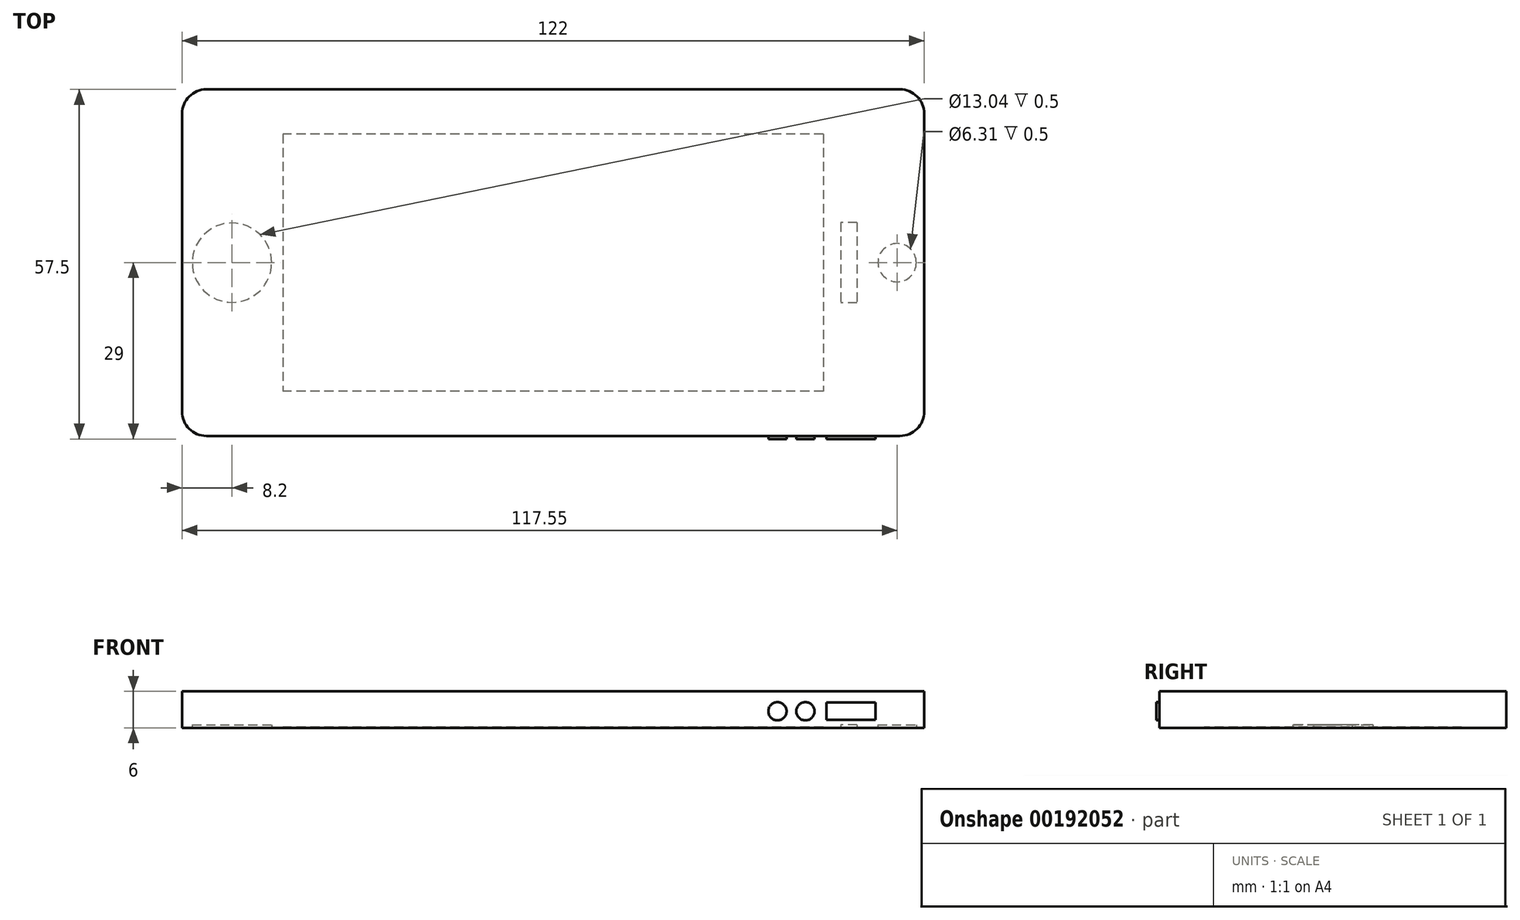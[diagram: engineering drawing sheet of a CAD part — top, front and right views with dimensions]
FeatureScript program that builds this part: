
annotation { "Feature Type Name" : "Feature", "Feature Type Description" : "" }
export const myFeature = defineFeature(function(context is Context, id is Id, definition is map)
    precondition{}
    {
        {
            var Q0;
            Q0=qCreatedBy(makeId("Top.planeOp"),FACE);
            var sketch = newSketch(context, id + "F0", { "sketchPlane" : qUnion([Q0])});
            skLineSegment(sketch, "E0.bottom", {"start": v(-61, 28.5) * mm, "end": v(61, 28.5) * mm});
            skLineSegment(sketch, "E0.top", {"start": v(-61, -28.5) * mm, "end": v(61, -28.5) * mm});
            skLineSegment(sketch, "E0.left", {"start": v(-61, 28.5) * mm, "end": v(-61, -28.5) * mm});
            skLineSegment(sketch, "E0.right", {"start": v(61, 28.5) * mm, "end": v(61, -28.5) * mm});
            skPoint(sketch, "E0.middle", {"position": v(0, 0) * mm});
            skSolve(sketch);
        }
        {
            var Q0;
            Q0=makeQuery(id+"F0.imprint","IMPRINT",FACE,{"disambiguationData":[TD([[makeQuery(id+"F0.imprint","IMPRINT",EDGE,{"derivedFrom":sQuery(id+"F0.wireOp",EDGE,"E0.bottom")}),-1.0]])]});
            extrude(context, id + "F1", {"entities" : qUnion([Q0]), "depth" : 6 * mm});
        }
        {
            var Q0;
            Q0=makeQuery(id+"F1.opExtrude","SWEPT_EDGE",EDGE,{"disambiguationData":[OSD([sQuery(id+"F0.wireOp",EDGE,"E0.bottom"),sQuery(id+"F0.wireOp",EDGE,"E0.right")])]});
            var Q1;
            Q1=makeQuery(id+"F1.opExtrude","SWEPT_EDGE",EDGE,{"disambiguationData":[OSD([sQuery(id+"F0.wireOp",EDGE,"E0.top"),sQuery(id+"F0.wireOp",EDGE,"E0.right")])]});
            var Q2;
            Q2=makeQuery(id+"F1.opExtrude","SWEPT_EDGE",EDGE,{"disambiguationData":[OSD([sQuery(id+"F0.wireOp",EDGE,"E0.bottom"),sQuery(id+"F0.wireOp",EDGE,"E0.left")])]});
            var Q3;
            Q3=makeQuery(id+"F1.opExtrude","SWEPT_EDGE",EDGE,{"disambiguationData":[OSD([sQuery(id+"F0.wireOp",EDGE,"E0.top"),sQuery(id+"F0.wireOp",EDGE,"E0.left")])]});
            fillet(context, id + "F2", {"entities" : qUnion([Q0, Q1, Q2, Q3]), "radius" : 4 * mm, "tangentPropagation" : true, "allowEdgeOverflow" : false});
        }
        {
            var Q0;
            Q0=makeQuery(id+"F1.opExtrude","SWEPT_FACE",FACE,{"disambiguationData":[OSD([sQuery(id+"F0.wireOp",EDGE,"E0.top")])]});
            var sketch = newSketch(context, id + "F3", { "sketchPlane" : qUnion([Q0])});
            skLineSegment(sketch, "E1.bottom", {"start": v(52.97, 1.29) * mm, "end": v(44.92, 1.29) * mm});
            skLineSegment(sketch, "E1.top", {"start": v(52.97, 4.16) * mm, "end": v(44.92, 4.16) * mm});
            skLineSegment(sketch, "E1.left", {"start": v(52.97, 1.29) * mm, "end": v(52.97, 4.16) * mm});
            skLineSegment(sketch, "E1.right", {"start": v(44.92, 1.29) * mm, "end": v(44.92, 4.16) * mm});
            skPoint(sketch, "E1.middle", {"position": v(48.94, 2.73) * mm});
            skCircle(sketch, "E2", {"center": v(41.47, 2.73) * mm, "radius": 1.5 * mm});
            skPoint(sketch, "E2.centerSnap0", {"position": v(44.92, 2.73) * mm});
            skCircle(sketch, "E3", {"center": v(36.87, 2.73) * mm, "radius": 1.5 * mm});
            skSolve(sketch);
        }
        {
            var Q0;
            Q0=makeQuery(id+"F3.imprint","IMPRINT",FACE,{"disambiguationData":[TD([[makeQuery(id+"F3.imprint","IMPRINT",EDGE,{"derivedFrom":sQuery(id+"F3.wireOp",EDGE,"E3")}),1.0]])]});
            var Q1;
            Q1=makeQuery(id+"F3.imprint","IMPRINT",FACE,{"disambiguationData":[TD([[makeQuery(id+"F3.imprint","IMPRINT",EDGE,{"derivedFrom":sQuery(id+"F3.wireOp",EDGE,"E2")}),1.0]])]});
            var Q2;
            Q2=makeQuery(id+"F3.imprint","IMPRINT",FACE,{"disambiguationData":[TD([[makeQuery(id+"F3.imprint","IMPRINT",EDGE,{"derivedFrom":sQuery(id+"F3.wireOp",EDGE,"E1.bottom")}),-1.0]])]});
            extrude(context, id + "F4", {"entities" : qUnion([Q0, Q1, Q2]), "operationType" : NewBodyOperationType.ADD, "depth" : 0.5 * mm});
        }
        {
            var Q0;
            Q0=makeQuery(id+"F1.opExtrude","CAP_FACE",FACE,{"disambiguationData":[OSD([sQuery(id+"F0.wireOp",EDGE,"E0.bottom"),sQuery(id+"F0.wireOp",EDGE,"E0.top"),sQuery(id+"F0.wireOp",EDGE,"E0.left"),sQuery(id+"F0.wireOp",EDGE,"E0.right")])],"isStart":true});
            var sketch = newSketch(context, id + "F5", { "sketchPlane" : qUnion([Q0])});
            skCircle(sketch, "E4", {"center": v(-52.8, 0) * mm, "radius": 6.52 * mm});
            skSolve(sketch);
        }
        {
            var Q0;
            Q0=makeQuery(id+"F5.imprint","IMPRINT",FACE,{"disambiguationData":[TD([[makeQuery(id+"F5.imprint","IMPRINT",EDGE,{"derivedFrom":sQuery(id+"F5.wireOp",EDGE,"E4")}),1.0]])]});
            extrude(context, id + "F6", {"entities" : qUnion([Q0]), "operationType" : NewBodyOperationType.REMOVE, "oppositeDirection" : true, "depth" : 0.5 * mm});
        }
        {
            var Q0;
            Q0=makeQuery(id+"F1.opExtrude","CAP_FACE",FACE,{"disambiguationData":[OSD([sQuery(id+"F0.wireOp",EDGE,"E0.bottom"),sQuery(id+"F0.wireOp",EDGE,"E0.top"),sQuery(id+"F0.wireOp",EDGE,"E0.left"),sQuery(id+"F0.wireOp",EDGE,"E0.right")])],"isStart":true});
            var sketch = newSketch(context, id + "F7", { "sketchPlane" : qUnion([Q0])});
            skLineSegment(sketch, "E5.bottom", {"start": v(44.4, -21.15) * mm, "end": v(-44.4, -21.15) * mm});
            skLineSegment(sketch, "E5.top", {"start": v(44.4, 21.15) * mm, "end": v(-44.4, 21.15) * mm});
            skLineSegment(sketch, "E5.left", {"start": v(44.4, -21.15) * mm, "end": v(44.4, 21.15) * mm});
            skLineSegment(sketch, "E5.right", {"start": v(-44.4, -21.15) * mm, "end": v(-44.4, 21.15) * mm});
            skPoint(sketch, "E5.middle", {"position": v(0, 0) * mm});
            skSolve(sketch);
        }
        {
            var Q0;
            Q0 = qSketchRegion(id + "F7", true);
            extrude(context, id + "F8", {"entities" : qUnion([Q0]), "operationType" : NewBodyOperationType.REMOVE, "oppositeDirection" : true, "depth" : 0.1 * mm});
        }
        {
            var Q0;
            Q0=makeQuery(id+"F1.opExtrude","CAP_FACE",FACE,{"disambiguationData":[OSD([sQuery(id+"F0.wireOp",EDGE,"E0.bottom"),sQuery(id+"F0.wireOp",EDGE,"E0.top"),sQuery(id+"F0.wireOp",EDGE,"E0.left"),sQuery(id+"F0.wireOp",EDGE,"E0.right")])],"isStart":true});
            var sketch = newSketch(context, id + "F9", { "sketchPlane" : qUnion([Q0])});
            skCircle(sketch, "E6", {"center": v(56.55, 0) * mm, "radius": 3.15 * mm});
            skLineSegment(sketch, "E7.bottom", {"start": v(49.95, -6.6) * mm, "end": v(47.25, -6.6) * mm});
            skLineSegment(sketch, "E7.top", {"start": v(49.95, 6.6) * mm, "end": v(47.25, 6.6) * mm});
            skLineSegment(sketch, "E7.left", {"start": v(49.95, -6.6) * mm, "end": v(49.95, 6.6) * mm});
            skLineSegment(sketch, "E7.right", {"start": v(47.25, -6.6) * mm, "end": v(47.25, 6.6) * mm});
            skPoint(sketch, "E7.middle", {"position": v(48.6, 0) * mm});
            skSolve(sketch);
        }
        {
            var Q0;
            Q0=makeQuery(id+"F9.imprint","IMPRINT",FACE,{"disambiguationData":[TD([[makeQuery(id+"F9.imprint","IMPRINT",EDGE,{"derivedFrom":sQuery(id+"F9.wireOp",EDGE,"E6")}),1.0]])]});
            var Q1;
            Q1=makeQuery(id+"F9.imprint","IMPRINT",FACE,{"disambiguationData":[TD([[makeQuery(id+"F9.imprint","IMPRINT",EDGE,{"derivedFrom":sQuery(id+"F9.wireOp",EDGE,"E7.bottom")}),-1.0]])]});
            extrude(context, id + "F10", {"entities" : qUnion([Q0, Q1]), "operationType" : NewBodyOperationType.REMOVE, "oppositeDirection" : true, "depth" : 0.5 * mm});
        }
    });
